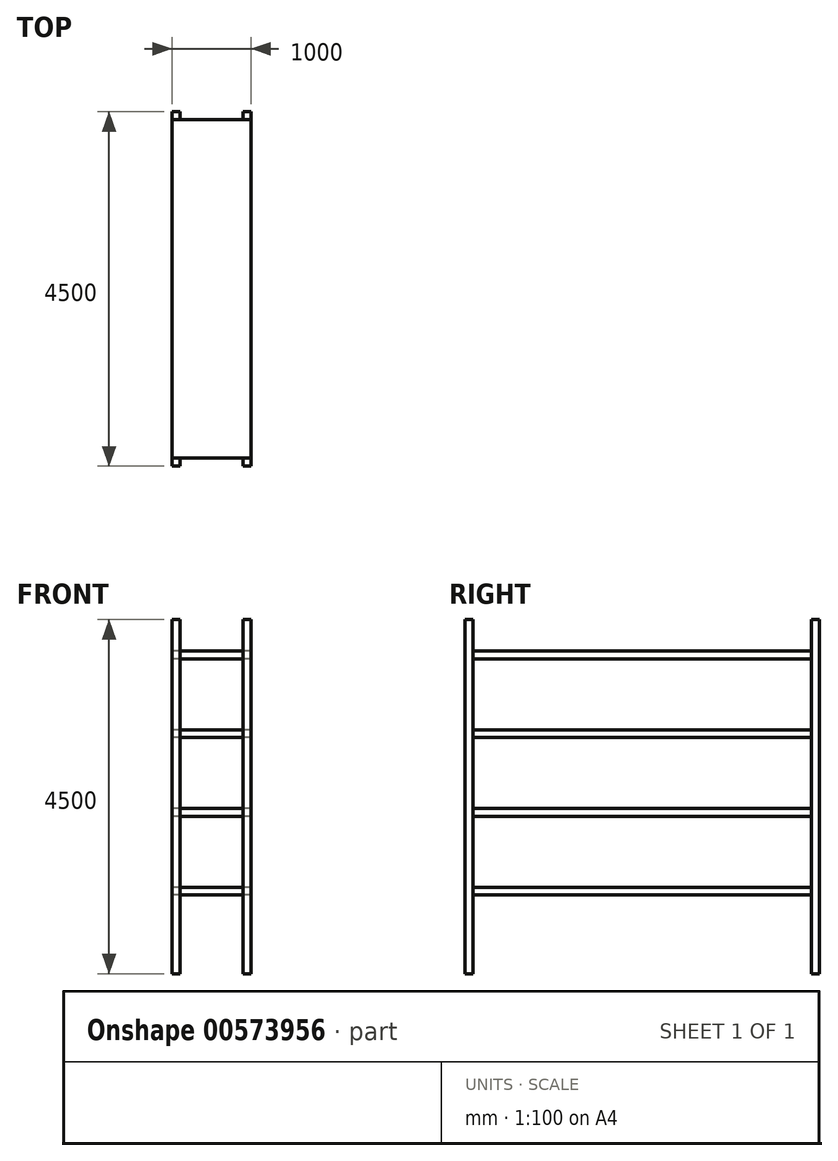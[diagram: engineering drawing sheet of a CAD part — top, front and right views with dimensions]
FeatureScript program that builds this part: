
annotation { "Feature Type Name" : "Feature", "Feature Type Description" : "" }
export const myFeature = defineFeature(function(context is Context, id is Id, definition is map)
    precondition{}
    {
        {
            var Q0;
            Q0=qCreatedBy(makeId("Top.planeOp"),FACE);
            var sketch = newSketch(context, id + "F0", { "sketchPlane" : qUnion([Q0])});
            skPoint(sketch, "E0.middle", {"position": v(0, 0) * mm});
            skLineSegment(sketch, "E1.bottom", {"start": v(-500, 2250) * mm, "end": v(-400, 2250) * mm});
            skLineSegment(sketch, "E1.top", {"start": v(-500, 2150) * mm, "end": v(-400, 2150) * mm});
            skLineSegment(sketch, "E1.left", {"start": v(-500, 2250) * mm, "end": v(-500, 2150) * mm});
            skLineSegment(sketch, "E1.right", {"start": v(-400, 2250) * mm, "end": v(-400, 2150) * mm});
            skLineSegment(sketch, "E2.bottom", {"start": v(500, 2250) * mm, "end": v(400, 2250) * mm});
            skLineSegment(sketch, "E2.top", {"start": v(500, 2150) * mm, "end": v(400, 2150) * mm});
            skLineSegment(sketch, "E2.left", {"start": v(500, 2250) * mm, "end": v(500, 2150) * mm});
            skLineSegment(sketch, "E2.right", {"start": v(400, 2250) * mm, "end": v(400, 2150) * mm});
            skLineSegment(sketch, "E3.bottom", {"start": v(-500, -2250) * mm, "end": v(-400, -2250) * mm});
            skLineSegment(sketch, "E3.top", {"start": v(-500, -2150) * mm, "end": v(-400, -2150) * mm});
            skLineSegment(sketch, "E3.left", {"start": v(-500, -2250) * mm, "end": v(-500, -2150) * mm});
            skLineSegment(sketch, "E3.right", {"start": v(-400, -2250) * mm, "end": v(-400, -2150) * mm});
            skLineSegment(sketch, "E4.bottom", {"start": v(500, -2250) * mm, "end": v(400, -2250) * mm});
            skLineSegment(sketch, "E4.top", {"start": v(500, -2150) * mm, "end": v(400, -2150) * mm});
            skLineSegment(sketch, "E4.left", {"start": v(500, -2250) * mm, "end": v(500, -2150) * mm});
            skLineSegment(sketch, "E4.right", {"start": v(400, -2250) * mm, "end": v(400, -2150) * mm});
            skSolve(sketch);
        }
        {
            var Q0;
            Q0=qCreatedBy(makeId("Top.planeOp"),FACE);
            cPlane(context, id + "F1", {"entities" : qUnion([Q0]), "cplaneType" : CPlaneType.OFFSET, "offset" : 1000 * mm, "width" : 150 * mm, "height" : 150 * mm});
        }
        {
            var Q0;
            Q0=qCreatedBy(makeId("Top.planeOp"),FACE);
            cPlane(context, id + "F2", {"entities" : qUnion([Q0]), "cplaneType" : CPlaneType.OFFSET, "offset" : 2000 * mm, "width" : 150 * mm, "height" : 150 * mm});
        }
        {
            var Q0;
            Q0=qCreatedBy(makeId("Top.planeOp"),FACE);
            cPlane(context, id + "F3", {"entities" : qUnion([Q0]), "cplaneType" : CPlaneType.OFFSET, "offset" : 3000 * mm, "width" : 150 * mm, "height" : 150 * mm});
        }
        {
            var Q0;
            Q0=qCreatedBy(makeId("Top.planeOp"),FACE);
            cPlane(context, id + "F4", {"entities" : qUnion([Q0]), "cplaneType" : CPlaneType.OFFSET, "offset" : 4000 * mm, "width" : 150 * mm, "height" : 150 * mm});
        }
        {
            var Q0;
            Q0=qCreatedBy(id+"F1.planeOp",FACE);
            var sketch = newSketch(context, id + "F5", { "sketchPlane" : qUnion([Q0])});
            skLineSegment(sketch, "E5.bottom", {"start": v(500, 2150) * mm, "end": v(-500, 2150) * mm});
            skLineSegment(sketch, "E5.top", {"start": v(500, -2150) * mm, "end": v(-500, -2150) * mm});
            skLineSegment(sketch, "E5.left", {"start": v(500, 2150) * mm, "end": v(500, -2150) * mm});
            skLineSegment(sketch, "E5.right", {"start": v(-500, 2150) * mm, "end": v(-500, -2150) * mm});
            skPoint(sketch, "E5.middle", {"position": v(0, 0) * mm});
            skSolve(sketch);
        }
        {
            var Q0;
            Q0=qCreatedBy(id+"F2.planeOp",FACE);
            var sketch = newSketch(context, id + "F6", { "sketchPlane" : qUnion([Q0])});
            skLineSegment(sketch, "E6.bottom", {"start": v(500, 2150) * mm, "end": v(-500, 2150) * mm});
            skLineSegment(sketch, "E6.top", {"start": v(500, -2150) * mm, "end": v(-500, -2150) * mm});
            skLineSegment(sketch, "E6.left", {"start": v(500, 2150) * mm, "end": v(500, -2150) * mm});
            skLineSegment(sketch, "E6.right", {"start": v(-500, 2150) * mm, "end": v(-500, -2150) * mm});
            skPoint(sketch, "E6.middle", {"position": v(0, 0) * mm});
            skSolve(sketch);
        }
        {
            var Q0;
            Q0=qCreatedBy(id+"F3.planeOp",FACE);
            var sketch = newSketch(context, id + "F7", { "sketchPlane" : qUnion([Q0])});
            skLineSegment(sketch, "E7.bottom", {"start": v(500, 2150) * mm, "end": v(-500, 2150) * mm});
            skLineSegment(sketch, "E7.top", {"start": v(500, -2150) * mm, "end": v(-500, -2150) * mm});
            skLineSegment(sketch, "E7.left", {"start": v(500, 2150) * mm, "end": v(500, -2150) * mm});
            skLineSegment(sketch, "E7.right", {"start": v(-500, 2150) * mm, "end": v(-500, -2150) * mm});
            skPoint(sketch, "E7.middle", {"position": v(0, 0) * mm});
            skSolve(sketch);
        }
        {
            var Q0;
            Q0=qCreatedBy(id+"F4.planeOp",FACE);
            var sketch = newSketch(context, id + "F8", { "sketchPlane" : qUnion([Q0])});
            skLineSegment(sketch, "E8.bottom", {"start": v(500, 2150) * mm, "end": v(-500, 2150) * mm});
            skLineSegment(sketch, "E8.top", {"start": v(500, -2150) * mm, "end": v(-500, -2150) * mm});
            skLineSegment(sketch, "E8.left", {"start": v(500, 2150) * mm, "end": v(500, -2150) * mm});
            skLineSegment(sketch, "E8.right", {"start": v(-500, 2150) * mm, "end": v(-500, -2150) * mm});
            skPoint(sketch, "E8.middle", {"position": v(0, 0) * mm});
            skSolve(sketch);
        }
        {
            var Q0;
            Q0 = qSketchRegion(id + "F0", true);
            extrude(context, id + "F9", {"entities" : qUnion([Q0]), "depth" : 4500 * mm, "offsetDistance" : 25 * mm});
        }
        {
            var Q0;
            Q0 = qSketchRegion(id + "F5", true);
            extrude(context, id + "F10", {"entities" : qUnion([Q0]), "depth" : 100 * mm, "offsetDistance" : 25 * mm});
        }
        {
            var Q0;
            Q0 = qSketchRegion(id + "F6", true);
            extrude(context, id + "F11", {"entities" : qUnion([Q0]), "depth" : 100 * mm, "offsetDistance" : 25 * mm});
        }
        {
            var Q0;
            Q0 = qSketchRegion(id + "F7", true);
            extrude(context, id + "F12", {"entities" : qUnion([Q0]), "depth" : 100 * mm, "offsetDistance" : 25 * mm});
        }
        {
            var Q0;
            Q0 = qSketchRegion(id + "F8", true);
            extrude(context, id + "F13", {"entities" : qUnion([Q0]), "depth" : 100 * mm, "offsetDistance" : 25 * mm});
        }
    });
